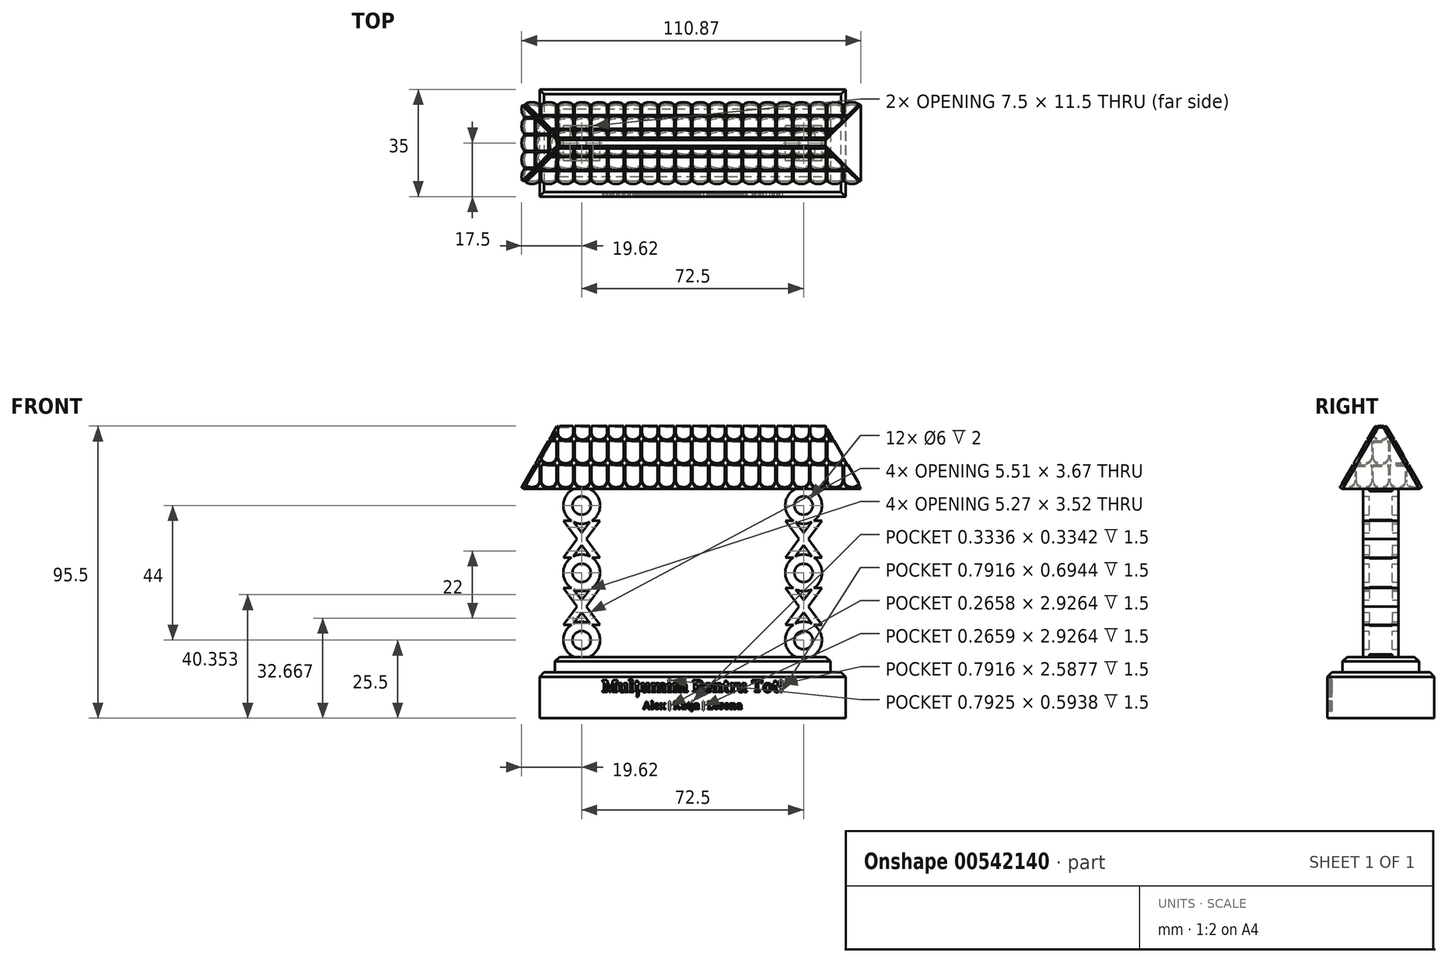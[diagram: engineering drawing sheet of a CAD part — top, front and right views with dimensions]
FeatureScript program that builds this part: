
annotation { "Feature Type Name" : "Feature", "Feature Type Description" : "" }
export const myFeature = defineFeature(function(context is Context, id is Id, definition is map)
    precondition{}
    {
        {
            var Q0;
            Q0=qCreatedBy(makeId("Top.planeOp"),FACE);
            var sketch = newSketch(context, id + "F0", { "sketchPlane" : qUnion([Q0])});
            skLineSegment(sketch, "E0.bottom", {"start": v(0, 0) * mm, "end": v(-100, 0) * mm});
            skLineSegment(sketch, "E0.top", {"start": v(0, 35) * mm, "end": v(-100, 35) * mm});
            skLineSegment(sketch, "E0.left", {"start": v(0, 0) * mm, "end": v(0, 35) * mm});
            skLineSegment(sketch, "E0.right", {"start": v(-100, 0) * mm, "end": v(-100, 35) * mm});
            skSolve(sketch);
        }
        {
            var Q0;
            Q0 = qSketchRegion(id + "F0", true);
            extrude(context, id + "F1", {"entities" : qUnion([Q0]), "depth" : 5 * mm, "offsetDistance" : 25 * mm});
        }
        {
            var Q0;
            Q0=makeQuery(id+"F1.opExtrude","CAP_FACE",FACE,{"disambiguationData":[OSD([sQuery(id+"F0.wireOp",EDGE,"E0.bottom"),sQuery(id+"F0.wireOp",EDGE,"E0.top"),sQuery(id+"F0.wireOp",EDGE,"E0.left"),sQuery(id+"F0.wireOp",EDGE,"E0.right")])],"isStart":false});
            var sketch = newSketch(context, id + "F2", { "sketchPlane" : qUnion([Q0])});
            skLineSegment(sketch, "E1.bottom", {"start": v(-5, 30) * mm, "end": v(-95, 30) * mm});
            skLineSegment(sketch, "E1.top", {"start": v(-5, 5) * mm, "end": v(-95, 5) * mm});
            skLineSegment(sketch, "E1.left", {"start": v(-5, 30) * mm, "end": v(-5, 5) * mm});
            skLineSegment(sketch, "E1.right", {"start": v(-95, 30) * mm, "end": v(-95, 5) * mm});
            skPoint(sketch, "E1.middle", {"position": v(-50, 17.5) * mm});
            skPoint(sketch, "E1.middle.positionSnap0", {"position": v(0, 17.5) * mm});
            skPoint(sketch, "E1.middle.positionSnap1", {"position": v(-50, 35) * mm});
            skPoint(sketch, "E1.centerSnap0", {"position": v(0, 17.5) * mm});
            skPoint(sketch, "E1.centerSnap1", {"position": v(-50, 35) * mm});
            skSolve(sketch);
        }
        {
            var Q0;
            Q0=makeQuery(id+"F2.imprint","IMPRINT",FACE,{"disambiguationData":[TD([[makeQuery(id+"F2.imprint","IMPRINT",EDGE,{"derivedFrom":sQuery(id+"F2.wireOp",EDGE,"E1.bottom")}),1.0]])]});
            extrude(context, id + "F3", {"entities" : qUnion([Q0]), "operationType" : NewBodyOperationType.ADD, "depth" : 5 * mm, "offsetDistance" : 25 * mm});
        }
        {
            var Q0;
            Q0=makeQuery(id+"F3.opExtrude","CAP_FACE",FACE,{"disambiguationData":[OSD([sQuery(id+"F2.wireOp",EDGE,"E1.bottom"),sQuery(id+"F2.wireOp",EDGE,"E1.top"),sQuery(id+"F2.wireOp",EDGE,"E1.left"),sQuery(id+"F2.wireOp",EDGE,"E1.right")])],"isStart":false});
            var sketch = newSketch(context, id + "F4", { "sketchPlane" : qUnion([Q0])});
            skLineSegment(sketch, "E2", {"start": v(-95, 17.5) * mm, "end": v(-5, 17.5) * mm, "construction": true});
            skLineSegment(sketch, "E3.bottom", {"start": v(-82.5, 21.25) * mm, "end": v(-90, 21.25) * mm});
            skLineSegment(sketch, "E3.top", {"start": v(-82.5, 13.75) * mm, "end": v(-90, 13.75) * mm});
            skLineSegment(sketch, "E3.left", {"start": v(-82.5, 21.25) * mm, "end": v(-82.5, 13.75) * mm});
            skLineSegment(sketch, "E3.right", {"start": v(-90, 21.25) * mm, "end": v(-90, 13.75) * mm});
            skPoint(sketch, "E3.middle", {"position": v(-86.25, 17.5) * mm});
            skLineSegment(sketch, "E4", {"start": v(-50, 30) * mm, "end": v(-50, 5) * mm, "construction": true});
            skLineSegment(sketch, "E5.MirrorCS", {"start": v(-17.5, 21.25) * mm, "end": v(-10, 21.25) * mm});
            skLineSegment(sketch, "E6.MirrorCS", {"start": v(-10, 21.25) * mm, "end": v(-10, 13.75) * mm});
            skLineSegment(sketch, "E7.MirrorCS", {"start": v(-17.5, 21.25) * mm, "end": v(-17.5, 13.75) * mm});
            skLineSegment(sketch, "E8.MirrorCS", {"start": v(-17.5, 13.75) * mm, "end": v(-10, 13.75) * mm});
            skSolve(sketch);
        }
        {
            var Q0;
            Q0 = qSketchRegion(id + "F4", true);
            extrude(context, id + "F5", {"entities" : qUnion([Q0]), "operationType" : NewBodyOperationType.ADD, "depth" : 55 * mm, "offsetDistance" : 25 * mm});
        }
        {
            var Q0;
            Q0=makeQuery(id+"F5.opExtrude","CAP_FACE",FACE,{"disambiguationData":[OSD([sQuery(id+"F4.wireOp",EDGE,"E3.bottom"),sQuery(id+"F4.wireOp",EDGE,"E3.top"),sQuery(id+"F4.wireOp",EDGE,"E3.left"),sQuery(id+"F4.wireOp",EDGE,"E3.right")])],"isStart":false});
            var sketch = newSketch(context, id + "F6", { "sketchPlane" : qUnion([Q0])});
            skLineSegment(sketch, "E9.bottom", {"start": v(-105, 30) * mm, "end": v(5, 30) * mm});
            skLineSegment(sketch, "E9.top", {"start": v(-105, 5) * mm, "end": v(5, 5) * mm});
            skLineSegment(sketch, "E9.left", {"start": v(-105, 30) * mm, "end": v(-105, 5) * mm});
            skLineSegment(sketch, "E9.right", {"start": v(5, 30) * mm, "end": v(5, 5) * mm});
            skSolve(sketch);
        }
        {
            var Q0;
            Q0 = qSketchRegion(id + "F6", true);
            extrude(context, id + "F7", {"entities" : qUnion([Q0]), "operationType" : NewBodyOperationType.ADD, "depth" : 20 * mm, "offsetDistance" : 25 * mm, "hasDraft" : true, "draftAngle" : 30 * degree, "draftPullDirection" : true});
        }
        {
            var Q0;
            Q0=makeQuery(id+"F5.opExtrude","SWEPT_FACE",FACE,{"disambiguationData":[OSD([sQuery(id+"F4.wireOp",EDGE,"E3.top")])]});
            var sketch = newSketch(context, id + "F8", { "sketchPlane" : qUnion([Q0])});
            skLineSegment(sketch, "E10", {"start": v(-86.25, 65) * mm, "end": v(-86.25, 10) * mm, "construction": true});
            skArc(sketch, "E11", {"start": v(-88.89, 54.11) * mm, "mid": v(-86.25, 53.5) * mm, "end": v(-83.61, 54.11) * mm});
            skCircle(sketch, "E12", {"center": v(-86.25, 59.5) * mm, "radius": 3 * mm});
            skLineSegment(sketch, "E13", {"start": v(-86.25, 50.6) * mm, "end": v(-88.89, 54.11) * mm});
            skLineSegment(sketch, "E14", {"start": v(-89.57, 54.5) * mm, "end": v(-92.25, 54.5) * mm});
            skLineSegment(sketch, "E15", {"start": v(-92.25, 54.5) * mm, "end": v(-87.75, 48.5) * mm});
            skLineSegment(sketch, "E16", {"start": v(-87.75, 48.5) * mm, "end": v(-92.25, 42.5) * mm});
            skLineSegment(sketch, "E17", {"start": v(-92.25, 42.5) * mm, "end": v(-89.25, 42.5) * mm});
            skLineSegment(sketch, "E18", {"start": v(-89, 42.83) * mm, "end": v(-86.25, 46.5) * mm});
            skLineSegment(sketch, "E19", {"start": v(-92.25, 54.5) * mm, "end": v(-92.25, 59.5) * mm, "construction": true});
            skLineSegment(sketch, "E20", {"start": v(-86.25, 48.5) * mm, "end": v(-94.11, 48.5) * mm, "construction": true});
            skLineSegment(sketch, "E21.MirrorCS", {"start": v(-83.5, 42.83) * mm, "end": v(-86.25, 46.5) * mm});
            skLineSegment(sketch, "E22.MirrorCS", {"start": v(-80.25, 42.5) * mm, "end": v(-82.94, 42.5) * mm});
            skLineSegment(sketch, "E23.MirrorCS", {"start": v(-84.75, 48.5) * mm, "end": v(-80.25, 42.5) * mm});
            skLineSegment(sketch, "E24.MirrorCS", {"start": v(-80.25, 54.5) * mm, "end": v(-84.75, 48.5) * mm});
            skLineSegment(sketch, "E25.MirrorCS", {"start": v(-86.25, 50.6) * mm, "end": v(-83.61, 54.11) * mm});
            skLineSegment(sketch, "E26.MirrorCS", {"start": v(-82.93, 54.5) * mm, "end": v(-80.25, 54.5) * mm});
            skLineSegment(sketch, "E27.0.1.0", {"start": v(-82.93, 32.5) * mm, "end": v(-80.25, 32.5) * mm});
            skLineSegment(sketch, "E27.0.1.1", {"start": v(-92.25, 32.5) * mm, "end": v(-87.75, 26.5) * mm});
            skLineSegment(sketch, "E27.0.1.2", {"start": v(-92.25, 32.5) * mm, "end": v(-92.25, 37.5) * mm, "construction": true});
            skLineSegment(sketch, "E27.0.1.3", {"start": v(-86.25, 26.5) * mm, "end": v(-94.11, 26.5) * mm, "construction": true});
            skLineSegment(sketch, "E27.0.1.4", {"start": v(-83.5, 20.83) * mm, "end": v(-86.25, 24.5) * mm});
            skLineSegment(sketch, "E27.0.1.5", {"start": v(-89, 20.83) * mm, "end": v(-86.25, 24.5) * mm});
            skCircle(sketch, "E27.0.1.6", {"center": v(-86.25, 37.5) * mm, "radius": 3 * mm});
            skLineSegment(sketch, "E27.0.1.7", {"start": v(-84.75, 26.5) * mm, "end": v(-80.25, 20.5) * mm});
            skLineSegment(sketch, "E27.0.1.8", {"start": v(-87.75, 26.5) * mm, "end": v(-92.25, 20.5) * mm});
            skLineSegment(sketch, "E27.0.1.9", {"start": v(-80.25, 20.5) * mm, "end": v(-82.94, 20.5) * mm});
            skLineSegment(sketch, "E27.0.1.10", {"start": v(-80.25, 32.5) * mm, "end": v(-84.75, 26.5) * mm});
            skLineSegment(sketch, "E27.0.1.11", {"start": v(-92.25, 20.5) * mm, "end": v(-89.56, 20.5) * mm});
            skArc(sketch, "E27.0.1.12", {"start": v(-89.56, 42.5) * mm, "mid": v(-92.25, 37.5) * mm, "end": v(-89.57, 32.5) * mm});
            skLineSegment(sketch, "E27.0.1.13", {"start": v(-86.25, 28.6) * mm, "end": v(-88.89, 32.11) * mm});
            skLineSegment(sketch, "E27.0.1.15", {"start": v(-86.25, 28.6) * mm, "end": v(-83.61, 32.11) * mm});
            skLineSegment(sketch, "E27.direction1", {"start": v(-92.25, 42.5) * mm, "end": v(-89.56, 42.5) * mm, "construction": true});
            skLineSegment(sketch, "E27.direction2", {"start": v(-92.25, 42.5) * mm, "end": v(-92.25, 20.5) * mm, "construction": true});
            skArc(sketch, "E28.trimOffspring", {"start": v(-82.93, 54.5) * mm, "mid": v(-86.25, 65.5) * mm, "end": v(-89.57, 54.5) * mm});
            skLineSegment(sketch, "E29.trimOffspring", {"start": v(-89.25, 42.5) * mm, "end": v(-83.25, 42.5) * mm, "construction": true});
            skLineSegment(sketch, "E30.trimOffspring", {"start": v(-82.94, 42.5) * mm, "end": v(-67.25, 42.5) * mm, "construction": true});
            skArc(sketch, "E31.trimOffspring", {"start": v(-83.5, 42.83) * mm, "mid": v(-86.25, 43.5) * mm, "end": v(-89, 42.83) * mm});
            skArc(sketch, "E32.trimOffspring", {"start": v(-82.93, 32.5) * mm, "mid": v(-80.25, 37.5) * mm, "end": v(-82.94, 42.5) * mm});
            skArc(sketch, "E33.trimOffspring", {"start": v(-88.89, 32.11) * mm, "mid": v(-86.25, 31.5) * mm, "end": v(-83.61, 32.11) * mm});
            skLineSegment(sketch, "E34", {"start": v(-89.57, 32.5) * mm, "end": v(-92.25, 32.5) * mm});
            skArc(sketch, "E35", {"start": v(-83.5, 20.83) * mm, "mid": v(-86.25, 21.5) * mm, "end": v(-89, 20.83) * mm});
            skCircle(sketch, "E36", {"center": v(-86.25, 15.5) * mm, "radius": 3 * mm});
            skArc(sketch, "E37.trimOffspring", {"start": v(-89.56, 20.5) * mm, "mid": v(-86.25, 9.5) * mm, "end": v(-82.94, 20.5) * mm});
            skSolve(sketch);
        }
        {
            var Q0;
            Q0 = qSketchRegion(id + "F8", true);
            var Q1;
            Q1=sQuery(id+"F8.wireOp",EDGE,"E11");
            var Q2;
            Q2=sQuery(id+"F8.wireOp",EDGE,"E12");
            var Q3;
            Q3=makeQuery(id+"F5.opExtrude","SWEPT_FACE",FACE,{"disambiguationData":[OSD([sQuery(id+"F4.wireOp",EDGE,"E3.bottom")])]});
            extrude(context, id + "F9", {"entities" : qUnion([Q0]), "operationType" : NewBodyOperationType.ADD, "surfaceEntities" : qUnion([Q1, Q2]), "depth" : 2 * mm, "offsetDistance" : 25 * mm, "hasSecondDirection" : true, "secondDirectionBound" : SecondDirectionBoundingType.UP_TO_SURFACE, "secondDirectionOppositeDirection" : true, "secondDirectionDepth" : 25 * mm, "secondDirectionBoundEntityFace" : qUnion([Q3]), "hasSecondDirectionOffset" : true, "secondDirectionOffsetDistance" : 2 * mm, "secondDirectionOffsetOppositeDirection" : true});
        }
        {
            var Q0;
            Q0=makeQuery(id+"F3.opExtrude","SWEPT_FACE",FACE,{"disambiguationData":[OSD([sQuery(id+"F2.wireOp",EDGE,"E1.right")])]});
            var Q1;
            Q1=makeQuery(id+"F3.opExtrude","SWEPT_FACE",FACE,{"disambiguationData":[OSD([sQuery(id+"F2.wireOp",EDGE,"E1.left")])]});
            cPlane(context, id + "F10", {"entities" : qUnion([Q0, Q1]), "cplaneType" : CPlaneType.MID_PLANE, "offset" : 25 * mm, "width" : 150 * mm, "height" : 150 * mm});
        }
        {
            var Q0;
            Q0=makeQuery(id+"F1.opExtrude","SWEPT_BODY",BODY,{"disambiguationData":[OSD([sQuery(id+"F0.wireOp",EDGE,"E0.bottom"),sQuery(id+"F0.wireOp",EDGE,"E0.top"),sQuery(id+"F0.wireOp",EDGE,"E0.left"),sQuery(id+"F0.wireOp",EDGE,"E0.right")])]});
            var Q1;
            Q1=qCreatedBy(id+"F10.planeOp",FACE);
            mirror(context, id + "F11", {"operationType" : NewBodyOperationType.ADD, "entities" : qUnion([Q0]), "mirrorPlane" : qUnion([Q1])});
        }
        {
            var Q0;
            Q0=makeQuery(id+"F9.boolean.opBoolean","SPLIT",FACE,{"disambiguationData":[TD([makeQuery(id+"F5.opExtrude","SWEPT_FACE",FACE,{"disambiguationData":[OSD([sQuery(id+"F4.wireOp",EDGE,"E3.right")])]}),makeQuery(id+"F9.opExtrude","SWEPT_FACE",FACE,{"disambiguationData":[OSD([sQuery(id+"F8.wireOp",EDGE,"E15")])]}),makeQuery(id+"F9.opExtrude","SWEPT_FACE",FACE,{"disambiguationData":[OSD([sQuery(id+"F8.wireOp",EDGE,"E16")])]})])],"derivedFrom":makeQuery(id+"F5.opExtrude","SWEPT_FACE",FACE,{"disambiguationData":[OSD([sQuery(id+"F4.wireOp",EDGE,"E3.top")])]})});
            var sketch = newSketch(context, id + "F12", { "sketchPlane" : qUnion([Q0])});
            skLineSegment(sketch, "E38", {"start": v(-90, 51.5) * mm, "end": v(-87.75, 48.5) * mm});
            skLineSegment(sketch, "E39", {"start": v(-87.75, 48.5) * mm, "end": v(-90, 45.5) * mm});
            skLineSegment(sketch, "E40", {"start": v(-90, 45.5) * mm, "end": v(-90, 51.5) * mm});
            skLineSegment(sketch, "E41", {"start": v(-87.75, 26.5) * mm, "end": v(-90, 29.5) * mm});
            skLineSegment(sketch, "E42", {"start": v(-90, 29.5) * mm, "end": v(-90, 23.5) * mm});
            skLineSegment(sketch, "E43", {"start": v(-90, 23.5) * mm, "end": v(-87.75, 26.5) * mm});
            skLineSegment(sketch, "E44", {"start": v(-86.25, 59.5) * mm, "end": v(-86.25, 15.5) * mm, "construction": true});
            skLineSegment(sketch, "E45.MirrorCS", {"start": v(-82.5, 23.5) * mm, "end": v(-84.75, 26.5) * mm});
            skLineSegment(sketch, "E46.MirrorCS", {"start": v(-82.5, 29.5) * mm, "end": v(-82.5, 23.5) * mm});
            skLineSegment(sketch, "E47.MirrorCS", {"start": v(-84.75, 26.5) * mm, "end": v(-82.5, 29.5) * mm});
            skLineSegment(sketch, "E48.MirrorCS", {"start": v(-82.5, 45.5) * mm, "end": v(-82.5, 51.5) * mm});
            skLineSegment(sketch, "E49.MirrorCS", {"start": v(-82.5, 51.5) * mm, "end": v(-84.75, 48.5) * mm});
            skLineSegment(sketch, "E50.MirrorCS", {"start": v(-84.75, 48.5) * mm, "end": v(-82.5, 45.5) * mm});
            skLineSegment(sketch, "E51", {"start": v(-50, 62.04) * mm, "end": v(-50, 26.06) * mm, "construction": true});
            skLineSegment(sketch, "E52.MirrorCS", {"start": v(-15.25, 26.5) * mm, "end": v(-17.5, 29.5) * mm});
            skLineSegment(sketch, "E53.MirrorCS", {"start": v(-17.5, 23.5) * mm, "end": v(-15.25, 26.5) * mm});
            skLineSegment(sketch, "E54.MirrorCS", {"start": v(-17.5, 29.5) * mm, "end": v(-17.5, 23.5) * mm});
            skLineSegment(sketch, "E55.MirrorCS", {"start": v(-17.5, 45.5) * mm, "end": v(-17.5, 51.5) * mm});
            skLineSegment(sketch, "E56.MirrorCS", {"start": v(-15.25, 48.5) * mm, "end": v(-17.5, 45.5) * mm});
            skLineSegment(sketch, "E57.MirrorCS", {"start": v(-17.5, 51.5) * mm, "end": v(-15.25, 48.5) * mm});
            skLineSegment(sketch, "E58.MirrorCS", {"start": v(-10, 23.5) * mm, "end": v(-12.25, 26.5) * mm});
            skLineSegment(sketch, "E59.MirrorCS", {"start": v(-10, 29.5) * mm, "end": v(-10, 23.5) * mm});
            skLineSegment(sketch, "E60.MirrorCS", {"start": v(-12.25, 26.5) * mm, "end": v(-10, 29.5) * mm});
            skLineSegment(sketch, "E61.MirrorCS", {"start": v(-10, 45.5) * mm, "end": v(-10, 51.5) * mm});
            skLineSegment(sketch, "E62.MirrorCS", {"start": v(-10, 51.5) * mm, "end": v(-12.25, 48.5) * mm});
            skLineSegment(sketch, "E63.MirrorCS", {"start": v(-12.25, 48.5) * mm, "end": v(-10, 45.5) * mm});
            skSolve(sketch);
        }
        {
            var Q0;
            Q0 = qSketchRegion(id + "F12", true);
            extrude(context, id + "F13", {"entities" : qUnion([Q0]), "operationType" : NewBodyOperationType.REMOVE, "oppositeDirection" : true, "depth" : 25 * mm, "offsetDistance" : 25 * mm});
        }
        {
            var Q0;
            Q0=makeQuery(id+"F7.opExtrude","SWEPT_FACE",FACE,{"disambiguationData":[OSD([sQuery(id+"F6.wireOp",EDGE,"E9.top")])]});
            var sketch = newSketch(context, id + "F14", { "sketchPlane" : qUnion([Q0])});
            skArc(sketch, "E64", {"start": v(-104.5, 59.8) * mm, "mid": v(-101.7, 58.92) * mm, "end": v(-100, 61.3) * mm});
            skLineSegment(sketch, "E65", {"start": v(-100, 61.3) * mm, "end": v(-100, 67.3) * mm});
            skLineSegment(sketch, "E66", {"start": v(-105, 61.3) * mm, "end": v(-105, 67.3) * mm});
            skLineSegment(sketch, "E67", {"start": v(-100, 67.3) * mm, "end": v(-100.75, 67.3) * mm});
            skArc(sketch, "E68.0.1.2", {"start": v(-105, 70.3) * mm, "mid": v(-102.5, 67.8) * mm, "end": v(-100, 70.3) * mm, "construction": true});
            skLineSegment(sketch, "E68.1.0.0", {"start": v(-94.5, 67.3) * mm, "end": v(-99.5, 67.3) * mm});
            skLineSegment(sketch, "E68.1.0.1", {"start": v(-94.5, 61.3) * mm, "end": v(-94.5, 67.3) * mm});
            skArc(sketch, "E68.1.0.2", {"start": v(-99.5, 61.3) * mm, "mid": v(-97, 58.8) * mm, "end": v(-94.5, 61.3) * mm});
            skLineSegment(sketch, "E68.1.0.3", {"start": v(-99.5, 61.3) * mm, "end": v(-99.5, 67.3) * mm});
            skLineSegment(sketch, "E68.1.1.0", {"start": v(-94.5, 76.3) * mm, "end": v(-96.25, 76.3) * mm});
            skLineSegment(sketch, "E68.1.1.1", {"start": v(-94.5, 70.3) * mm, "end": v(-94.5, 76.3) * mm});
            skArc(sketch, "E68.1.1.2", {"start": v(-99.46, 69.87) * mm, "mid": v(-96.79, 67.8) * mm, "end": v(-94.5, 70.3) * mm});
            skLineSegment(sketch, "E68.1.2.1", {"start": v(-94.5, 79.3) * mm, "end": v(-94.5, 79.8) * mm});
            skArc(sketch, "E68.1.2.2", {"start": v(-95.86, 77.07) * mm, "mid": v(-94.87, 77.99) * mm, "end": v(-94.5, 79.3) * mm});
            skLineSegment(sketch, "E68.2.0.0", {"start": v(-89, 67.3) * mm, "end": v(-94, 67.3) * mm});
            skLineSegment(sketch, "E68.2.0.1", {"start": v(-89, 61.3) * mm, "end": v(-89, 67.3) * mm});
            skArc(sketch, "E68.2.0.2", {"start": v(-94, 61.3) * mm, "mid": v(-91.5, 58.8) * mm, "end": v(-89, 61.3) * mm});
            skLineSegment(sketch, "E68.2.0.3", {"start": v(-94, 61.3) * mm, "end": v(-94, 67.3) * mm});
            skLineSegment(sketch, "E68.2.1.0", {"start": v(-89, 76.3) * mm, "end": v(-94, 76.3) * mm});
            skLineSegment(sketch, "E68.2.1.1", {"start": v(-89, 70.3) * mm, "end": v(-89, 76.3) * mm});
            skArc(sketch, "E68.2.1.2", {"start": v(-94, 70.3) * mm, "mid": v(-91.5, 67.8) * mm, "end": v(-89, 70.3) * mm});
            skLineSegment(sketch, "E68.2.1.3", {"start": v(-94, 70.3) * mm, "end": v(-94, 76.3) * mm});
            skLineSegment(sketch, "E68.2.2.1", {"start": v(-89, 79.3) * mm, "end": v(-89, 81.89) * mm});
            skArc(sketch, "E68.2.2.2", {"start": v(-94, 79.3) * mm, "mid": v(-91.5, 76.8) * mm, "end": v(-89, 79.3) * mm});
            skLineSegment(sketch, "E68.2.2.3", {"start": v(-94, 79.3) * mm, "end": v(-94, 80.8) * mm});
            skLineSegment(sketch, "E68.3.0.0", {"start": v(-83.5, 67.3) * mm, "end": v(-88.5, 67.3) * mm});
            skLineSegment(sketch, "E68.3.0.1", {"start": v(-83.5, 61.3) * mm, "end": v(-83.5, 67.3) * mm});
            skArc(sketch, "E68.3.0.2", {"start": v(-88.5, 61.3) * mm, "mid": v(-86, 58.8) * mm, "end": v(-83.5, 61.3) * mm});
            skLineSegment(sketch, "E68.3.0.3", {"start": v(-88.5, 61.3) * mm, "end": v(-88.5, 67.3) * mm});
            skLineSegment(sketch, "E68.3.1.0", {"start": v(-83.5, 76.3) * mm, "end": v(-88.5, 76.3) * mm});
            skLineSegment(sketch, "E68.3.1.1", {"start": v(-83.5, 70.3) * mm, "end": v(-83.5, 76.3) * mm});
            skArc(sketch, "E68.3.1.2", {"start": v(-88.5, 70.3) * mm, "mid": v(-86, 67.8) * mm, "end": v(-83.5, 70.3) * mm});
            skLineSegment(sketch, "E68.3.1.3", {"start": v(-88.5, 70.3) * mm, "end": v(-88.5, 76.3) * mm});
            skLineSegment(sketch, "E68.3.2.1", {"start": v(-83.5, 79.3) * mm, "end": v(-83.5, 81.89) * mm});
            skArc(sketch, "E68.3.2.2", {"start": v(-88.5, 79.3) * mm, "mid": v(-86, 76.8) * mm, "end": v(-83.5, 79.3) * mm});
            skLineSegment(sketch, "E68.3.2.3", {"start": v(-88.5, 79.3) * mm, "end": v(-88.5, 81.89) * mm});
            skLineSegment(sketch, "E68.4.0.0", {"start": v(-78, 67.3) * mm, "end": v(-83, 67.3) * mm});
            skLineSegment(sketch, "E68.4.0.1", {"start": v(-78, 61.3) * mm, "end": v(-78, 67.3) * mm});
            skArc(sketch, "E68.4.0.2", {"start": v(-83, 61.3) * mm, "mid": v(-80.5, 58.8) * mm, "end": v(-78, 61.3) * mm});
            skLineSegment(sketch, "E68.4.0.3", {"start": v(-83, 61.3) * mm, "end": v(-83, 67.3) * mm});
            skLineSegment(sketch, "E68.4.1.0", {"start": v(-78, 76.3) * mm, "end": v(-83, 76.3) * mm});
            skLineSegment(sketch, "E68.4.1.1", {"start": v(-78, 70.3) * mm, "end": v(-78, 76.3) * mm});
            skArc(sketch, "E68.4.1.2", {"start": v(-83, 70.3) * mm, "mid": v(-80.5, 67.8) * mm, "end": v(-78, 70.3) * mm});
            skLineSegment(sketch, "E68.4.1.3", {"start": v(-83, 70.3) * mm, "end": v(-83, 76.3) * mm});
            skLineSegment(sketch, "E68.4.2.1", {"start": v(-78, 79.3) * mm, "end": v(-78, 81.89) * mm});
            skArc(sketch, "E68.4.2.2", {"start": v(-83, 79.3) * mm, "mid": v(-80.5, 76.8) * mm, "end": v(-78, 79.3) * mm});
            skLineSegment(sketch, "E68.4.2.3", {"start": v(-83, 79.3) * mm, "end": v(-83, 81.89) * mm});
            skLineSegment(sketch, "E68.5.0.0", {"start": v(-72.5, 67.3) * mm, "end": v(-77.5, 67.3) * mm});
            skLineSegment(sketch, "E68.5.0.1", {"start": v(-72.5, 61.3) * mm, "end": v(-72.5, 67.3) * mm});
            skArc(sketch, "E68.5.0.2", {"start": v(-77.5, 61.3) * mm, "mid": v(-75, 58.8) * mm, "end": v(-72.5, 61.3) * mm});
            skLineSegment(sketch, "E68.5.0.3", {"start": v(-77.5, 61.3) * mm, "end": v(-77.5, 67.3) * mm});
            skLineSegment(sketch, "E68.5.1.0", {"start": v(-72.5, 76.3) * mm, "end": v(-77.5, 76.3) * mm});
            skLineSegment(sketch, "E68.5.1.1", {"start": v(-72.5, 70.3) * mm, "end": v(-72.5, 76.3) * mm});
            skArc(sketch, "E68.5.1.2", {"start": v(-77.5, 70.3) * mm, "mid": v(-75, 67.8) * mm, "end": v(-72.5, 70.3) * mm});
            skLineSegment(sketch, "E68.5.1.3", {"start": v(-77.5, 70.3) * mm, "end": v(-77.5, 76.3) * mm});
            skLineSegment(sketch, "E68.5.2.1", {"start": v(-72.5, 79.3) * mm, "end": v(-72.5, 81.89) * mm});
            skArc(sketch, "E68.5.2.2", {"start": v(-77.5, 79.3) * mm, "mid": v(-75, 76.8) * mm, "end": v(-72.5, 79.3) * mm});
            skLineSegment(sketch, "E68.5.2.3", {"start": v(-77.5, 79.3) * mm, "end": v(-77.5, 81.89) * mm});
            skLineSegment(sketch, "E68.6.0.0", {"start": v(-67, 67.3) * mm, "end": v(-72, 67.3) * mm});
            skLineSegment(sketch, "E68.6.0.1", {"start": v(-67, 61.3) * mm, "end": v(-67, 67.3) * mm});
            skArc(sketch, "E68.6.0.2", {"start": v(-72, 61.3) * mm, "mid": v(-69.5, 58.8) * mm, "end": v(-67, 61.3) * mm});
            skLineSegment(sketch, "E68.6.0.3", {"start": v(-72, 61.3) * mm, "end": v(-72, 67.3) * mm});
            skLineSegment(sketch, "E68.6.1.0", {"start": v(-67, 76.3) * mm, "end": v(-72, 76.3) * mm});
            skLineSegment(sketch, "E68.6.1.1", {"start": v(-67, 70.3) * mm, "end": v(-67, 76.3) * mm});
            skArc(sketch, "E68.6.1.2", {"start": v(-72, 70.3) * mm, "mid": v(-69.5, 67.8) * mm, "end": v(-67, 70.3) * mm});
            skLineSegment(sketch, "E68.6.1.3", {"start": v(-72, 70.3) * mm, "end": v(-72, 76.3) * mm});
            skLineSegment(sketch, "E68.6.2.1", {"start": v(-67, 79.3) * mm, "end": v(-67, 81.89) * mm});
            skArc(sketch, "E68.6.2.2", {"start": v(-72, 79.3) * mm, "mid": v(-69.5, 76.8) * mm, "end": v(-67, 79.3) * mm});
            skLineSegment(sketch, "E68.6.2.3", {"start": v(-72, 79.3) * mm, "end": v(-72, 81.89) * mm});
            skLineSegment(sketch, "E68.7.0.0", {"start": v(-61.5, 67.3) * mm, "end": v(-66.5, 67.3) * mm});
            skLineSegment(sketch, "E68.7.0.1", {"start": v(-61.5, 61.3) * mm, "end": v(-61.5, 67.3) * mm});
            skArc(sketch, "E68.7.0.2", {"start": v(-66.5, 61.3) * mm, "mid": v(-64, 58.8) * mm, "end": v(-61.5, 61.3) * mm});
            skLineSegment(sketch, "E68.7.0.3", {"start": v(-66.5, 61.3) * mm, "end": v(-66.5, 67.3) * mm});
            skLineSegment(sketch, "E68.7.1.0", {"start": v(-61.5, 76.3) * mm, "end": v(-66.5, 76.3) * mm});
            skLineSegment(sketch, "E68.7.1.1", {"start": v(-61.5, 70.3) * mm, "end": v(-61.5, 76.3) * mm});
            skArc(sketch, "E68.7.1.2", {"start": v(-66.5, 70.3) * mm, "mid": v(-64, 67.8) * mm, "end": v(-61.5, 70.3) * mm});
            skLineSegment(sketch, "E68.7.1.3", {"start": v(-66.5, 70.3) * mm, "end": v(-66.5, 76.3) * mm});
            skLineSegment(sketch, "E68.7.2.1", {"start": v(-61.5, 79.3) * mm, "end": v(-61.5, 81.89) * mm});
            skArc(sketch, "E68.7.2.2", {"start": v(-66.5, 79.3) * mm, "mid": v(-64, 76.8) * mm, "end": v(-61.5, 79.3) * mm});
            skLineSegment(sketch, "E68.7.2.3", {"start": v(-66.5, 79.3) * mm, "end": v(-66.5, 81.89) * mm});
            skLineSegment(sketch, "E68.8.0.0", {"start": v(-56, 67.3) * mm, "end": v(-61, 67.3) * mm});
            skLineSegment(sketch, "E68.8.0.1", {"start": v(-56, 61.3) * mm, "end": v(-56, 67.3) * mm});
            skArc(sketch, "E68.8.0.2", {"start": v(-61, 61.3) * mm, "mid": v(-58.5, 58.8) * mm, "end": v(-56, 61.3) * mm});
            skLineSegment(sketch, "E68.8.0.3", {"start": v(-61, 61.3) * mm, "end": v(-61, 67.3) * mm});
            skLineSegment(sketch, "E68.8.1.0", {"start": v(-56, 76.3) * mm, "end": v(-61, 76.3) * mm});
            skLineSegment(sketch, "E68.8.1.1", {"start": v(-56, 70.3) * mm, "end": v(-56, 76.3) * mm});
            skArc(sketch, "E68.8.1.2", {"start": v(-61, 70.3) * mm, "mid": v(-58.5, 67.8) * mm, "end": v(-56, 70.3) * mm});
            skLineSegment(sketch, "E68.8.1.3", {"start": v(-61, 70.3) * mm, "end": v(-61, 76.3) * mm});
            skLineSegment(sketch, "E68.8.2.1", {"start": v(-56, 79.3) * mm, "end": v(-56, 81.89) * mm});
            skArc(sketch, "E68.8.2.2", {"start": v(-61, 79.3) * mm, "mid": v(-58.5, 76.8) * mm, "end": v(-56, 79.3) * mm});
            skLineSegment(sketch, "E68.8.2.3", {"start": v(-61, 79.3) * mm, "end": v(-61, 81.89) * mm});
            skLineSegment(sketch, "E68.9.0.0", {"start": v(-50.5, 67.3) * mm, "end": v(-55.5, 67.3) * mm});
            skLineSegment(sketch, "E68.9.0.1", {"start": v(-50.5, 61.3) * mm, "end": v(-50.5, 67.3) * mm});
            skArc(sketch, "E68.9.0.2", {"start": v(-55.5, 61.3) * mm, "mid": v(-53, 58.8) * mm, "end": v(-50.5, 61.3) * mm});
            skLineSegment(sketch, "E68.9.0.3", {"start": v(-55.5, 61.3) * mm, "end": v(-55.5, 67.3) * mm});
            skLineSegment(sketch, "E68.9.1.0", {"start": v(-50.5, 76.3) * mm, "end": v(-55.5, 76.3) * mm});
            skLineSegment(sketch, "E68.9.1.1", {"start": v(-50.5, 70.3) * mm, "end": v(-50.5, 76.3) * mm});
            skArc(sketch, "E68.9.1.2", {"start": v(-55.5, 70.3) * mm, "mid": v(-53, 67.8) * mm, "end": v(-50.5, 70.3) * mm});
            skLineSegment(sketch, "E68.9.1.3", {"start": v(-55.5, 70.3) * mm, "end": v(-55.5, 76.3) * mm});
            skLineSegment(sketch, "E68.9.2.1", {"start": v(-50.5, 79.3) * mm, "end": v(-50.5, 81.89) * mm});
            skArc(sketch, "E68.9.2.2", {"start": v(-55.5, 79.3) * mm, "mid": v(-53, 76.8) * mm, "end": v(-50.5, 79.3) * mm});
            skLineSegment(sketch, "E68.9.2.3", {"start": v(-55.5, 79.3) * mm, "end": v(-55.5, 81.89) * mm});
            skLineSegment(sketch, "E68.10.0.0", {"start": v(-45, 67.3) * mm, "end": v(-50, 67.3) * mm});
            skLineSegment(sketch, "E68.10.0.1", {"start": v(-45, 61.3) * mm, "end": v(-45, 67.3) * mm});
            skArc(sketch, "E68.10.0.2", {"start": v(-50, 61.3) * mm, "mid": v(-47.5, 58.8) * mm, "end": v(-45, 61.3) * mm});
            skLineSegment(sketch, "E68.10.0.3", {"start": v(-50, 61.3) * mm, "end": v(-50, 67.3) * mm});
            skLineSegment(sketch, "E68.10.1.0", {"start": v(-45, 76.3) * mm, "end": v(-50, 76.3) * mm});
            skLineSegment(sketch, "E68.10.1.1", {"start": v(-45, 70.3) * mm, "end": v(-45, 76.3) * mm});
            skArc(sketch, "E68.10.1.2", {"start": v(-50, 70.3) * mm, "mid": v(-47.5, 67.8) * mm, "end": v(-45, 70.3) * mm});
            skLineSegment(sketch, "E68.10.1.3", {"start": v(-50, 70.3) * mm, "end": v(-50, 76.3) * mm});
            skLineSegment(sketch, "E68.10.2.1", {"start": v(-45, 79.3) * mm, "end": v(-45, 81.89) * mm});
            skArc(sketch, "E68.10.2.2", {"start": v(-50, 79.3) * mm, "mid": v(-47.5, 76.8) * mm, "end": v(-45, 79.3) * mm});
            skLineSegment(sketch, "E68.10.2.3", {"start": v(-50, 79.3) * mm, "end": v(-50, 81.89) * mm});
            skLineSegment(sketch, "E68.11.0.0", {"start": v(-39.5, 67.3) * mm, "end": v(-44.5, 67.3) * mm});
            skLineSegment(sketch, "E68.11.0.1", {"start": v(-39.5, 61.3) * mm, "end": v(-39.5, 67.3) * mm});
            skArc(sketch, "E68.11.0.2", {"start": v(-44.5, 61.3) * mm, "mid": v(-42, 58.8) * mm, "end": v(-39.5, 61.3) * mm});
            skLineSegment(sketch, "E68.11.0.3", {"start": v(-44.5, 61.3) * mm, "end": v(-44.5, 67.3) * mm});
            skLineSegment(sketch, "E68.11.1.0", {"start": v(-39.5, 76.3) * mm, "end": v(-44.5, 76.3) * mm});
            skLineSegment(sketch, "E68.11.1.1", {"start": v(-39.5, 70.3) * mm, "end": v(-39.5, 76.3) * mm});
            skArc(sketch, "E68.11.1.2", {"start": v(-44.5, 70.3) * mm, "mid": v(-42, 67.8) * mm, "end": v(-39.5, 70.3) * mm});
            skLineSegment(sketch, "E68.11.1.3", {"start": v(-44.5, 70.3) * mm, "end": v(-44.5, 76.3) * mm});
            skLineSegment(sketch, "E68.11.2.1", {"start": v(-39.5, 79.3) * mm, "end": v(-39.5, 81.89) * mm});
            skArc(sketch, "E68.11.2.2", {"start": v(-44.5, 79.3) * mm, "mid": v(-42, 76.8) * mm, "end": v(-39.5, 79.3) * mm});
            skLineSegment(sketch, "E68.11.2.3", {"start": v(-44.5, 79.3) * mm, "end": v(-44.5, 81.89) * mm});
            skLineSegment(sketch, "E68.12.0.0", {"start": v(-34, 67.3) * mm, "end": v(-39, 67.3) * mm});
            skLineSegment(sketch, "E68.12.0.1", {"start": v(-34, 61.3) * mm, "end": v(-34, 67.3) * mm});
            skArc(sketch, "E68.12.0.2", {"start": v(-39, 61.3) * mm, "mid": v(-36.5, 58.8) * mm, "end": v(-34, 61.3) * mm});
            skLineSegment(sketch, "E68.12.0.3", {"start": v(-39, 61.3) * mm, "end": v(-39, 67.3) * mm});
            skLineSegment(sketch, "E68.12.1.0", {"start": v(-34, 76.3) * mm, "end": v(-39, 76.3) * mm});
            skLineSegment(sketch, "E68.12.1.1", {"start": v(-34, 70.3) * mm, "end": v(-34, 76.3) * mm});
            skArc(sketch, "E68.12.1.2", {"start": v(-39, 70.3) * mm, "mid": v(-36.5, 67.8) * mm, "end": v(-34, 70.3) * mm});
            skLineSegment(sketch, "E68.12.1.3", {"start": v(-39, 70.3) * mm, "end": v(-39, 76.3) * mm});
            skLineSegment(sketch, "E68.12.2.1", {"start": v(-34, 79.3) * mm, "end": v(-34, 81.89) * mm});
            skArc(sketch, "E68.12.2.2", {"start": v(-39, 79.3) * mm, "mid": v(-36.5, 76.8) * mm, "end": v(-34, 79.3) * mm});
            skLineSegment(sketch, "E68.12.2.3", {"start": v(-39, 79.3) * mm, "end": v(-39, 81.89) * mm});
            skLineSegment(sketch, "E68.13.0.0", {"start": v(-28.5, 67.3) * mm, "end": v(-33.5, 67.3) * mm});
            skLineSegment(sketch, "E68.13.0.1", {"start": v(-28.5, 61.3) * mm, "end": v(-28.5, 67.3) * mm});
            skArc(sketch, "E68.13.0.2", {"start": v(-33.5, 61.3) * mm, "mid": v(-31, 58.8) * mm, "end": v(-28.5, 61.3) * mm});
            skLineSegment(sketch, "E68.13.0.3", {"start": v(-33.5, 61.3) * mm, "end": v(-33.5, 67.3) * mm});
            skLineSegment(sketch, "E68.13.1.0", {"start": v(-28.5, 76.3) * mm, "end": v(-33.5, 76.3) * mm});
            skLineSegment(sketch, "E68.13.1.1", {"start": v(-28.5, 70.3) * mm, "end": v(-28.5, 76.3) * mm});
            skArc(sketch, "E68.13.1.2", {"start": v(-33.5, 70.3) * mm, "mid": v(-31, 67.8) * mm, "end": v(-28.5, 70.3) * mm});
            skLineSegment(sketch, "E68.13.1.3", {"start": v(-33.5, 70.3) * mm, "end": v(-33.5, 76.3) * mm});
            skLineSegment(sketch, "E68.13.2.1", {"start": v(-28.5, 79.3) * mm, "end": v(-28.5, 81.89) * mm});
            skArc(sketch, "E68.13.2.2", {"start": v(-33.5, 79.3) * mm, "mid": v(-31, 76.8) * mm, "end": v(-28.5, 79.3) * mm});
            skLineSegment(sketch, "E68.13.2.3", {"start": v(-33.5, 79.3) * mm, "end": v(-33.5, 81.89) * mm});
            skLineSegment(sketch, "E68.14.0.0", {"start": v(-23, 67.3) * mm, "end": v(-28, 67.3) * mm});
            skLineSegment(sketch, "E68.14.0.1", {"start": v(-23, 61.3) * mm, "end": v(-23, 67.3) * mm});
            skArc(sketch, "E68.14.0.2", {"start": v(-28, 61.3) * mm, "mid": v(-25.5, 58.8) * mm, "end": v(-23, 61.3) * mm});
            skLineSegment(sketch, "E68.14.0.3", {"start": v(-28, 61.3) * mm, "end": v(-28, 67.3) * mm});
            skLineSegment(sketch, "E68.14.1.0", {"start": v(-23, 76.3) * mm, "end": v(-28, 76.3) * mm});
            skLineSegment(sketch, "E68.14.1.1", {"start": v(-23, 70.3) * mm, "end": v(-23, 76.3) * mm});
            skArc(sketch, "E68.14.1.2", {"start": v(-28, 70.3) * mm, "mid": v(-25.5, 67.8) * mm, "end": v(-23, 70.3) * mm});
            skLineSegment(sketch, "E68.14.1.3", {"start": v(-28, 70.3) * mm, "end": v(-28, 76.3) * mm});
            skLineSegment(sketch, "E68.14.2.1", {"start": v(-23, 79.3) * mm, "end": v(-23, 81.89) * mm});
            skArc(sketch, "E68.14.2.2", {"start": v(-28, 79.3) * mm, "mid": v(-25.5, 76.8) * mm, "end": v(-23, 79.3) * mm});
            skLineSegment(sketch, "E68.14.2.3", {"start": v(-28, 79.3) * mm, "end": v(-28, 81.89) * mm});
            skLineSegment(sketch, "E68.15.0.0", {"start": v(-17.5, 67.3) * mm, "end": v(-22.5, 67.3) * mm});
            skLineSegment(sketch, "E68.15.0.1", {"start": v(-17.5, 61.3) * mm, "end": v(-17.5, 67.3) * mm});
            skArc(sketch, "E68.15.0.2", {"start": v(-22.5, 61.3) * mm, "mid": v(-20, 58.8) * mm, "end": v(-17.5, 61.3) * mm});
            skLineSegment(sketch, "E68.15.0.3", {"start": v(-22.5, 61.3) * mm, "end": v(-22.5, 67.3) * mm});
            skLineSegment(sketch, "E68.15.1.0", {"start": v(-17.5, 76.3) * mm, "end": v(-22.5, 76.3) * mm});
            skLineSegment(sketch, "E68.15.1.1", {"start": v(-17.5, 70.3) * mm, "end": v(-17.5, 76.3) * mm});
            skArc(sketch, "E68.15.1.2", {"start": v(-22.5, 70.3) * mm, "mid": v(-20, 67.8) * mm, "end": v(-17.5, 70.3) * mm});
            skLineSegment(sketch, "E68.15.1.3", {"start": v(-22.5, 70.3) * mm, "end": v(-22.5, 76.3) * mm});
            skLineSegment(sketch, "E68.15.2.1", {"start": v(-17.5, 79.3) * mm, "end": v(-17.5, 81.89) * mm});
            skArc(sketch, "E68.15.2.2", {"start": v(-22.5, 79.3) * mm, "mid": v(-20, 76.8) * mm, "end": v(-17.5, 79.3) * mm});
            skLineSegment(sketch, "E68.15.2.3", {"start": v(-22.5, 79.3) * mm, "end": v(-22.5, 81.89) * mm});
            skLineSegment(sketch, "E68.16.0.0", {"start": v(-12, 67.3) * mm, "end": v(-17, 67.3) * mm});
            skLineSegment(sketch, "E68.16.0.1", {"start": v(-12, 61.3) * mm, "end": v(-12, 67.3) * mm});
            skArc(sketch, "E68.16.0.2", {"start": v(-17, 61.3) * mm, "mid": v(-14.5, 58.8) * mm, "end": v(-12, 61.3) * mm});
            skLineSegment(sketch, "E68.16.0.3", {"start": v(-17, 61.3) * mm, "end": v(-17, 67.3) * mm});
            skLineSegment(sketch, "E68.16.1.0", {"start": v(-12, 76.3) * mm, "end": v(-17, 76.3) * mm});
            skLineSegment(sketch, "E68.16.1.1", {"start": v(-12, 70.3) * mm, "end": v(-12, 76.3) * mm});
            skArc(sketch, "E68.16.1.2", {"start": v(-17, 70.3) * mm, "mid": v(-14.5, 67.8) * mm, "end": v(-12, 70.3) * mm});
            skLineSegment(sketch, "E68.16.1.3", {"start": v(-17, 70.3) * mm, "end": v(-17, 76.3) * mm});
            skLineSegment(sketch, "E68.16.2.1", {"start": v(-12, 79.3) * mm, "end": v(-12, 81.89) * mm});
            skArc(sketch, "E68.16.2.2", {"start": v(-17, 79.3) * mm, "mid": v(-14.5, 76.8) * mm, "end": v(-12, 79.3) * mm});
            skLineSegment(sketch, "E68.16.2.3", {"start": v(-17, 79.3) * mm, "end": v(-17, 81.89) * mm});
            skLineSegment(sketch, "E68.17.0.0", {"start": v(-6.5, 67.3) * mm, "end": v(-11.5, 67.3) * mm});
            skLineSegment(sketch, "E68.17.0.1", {"start": v(-6.5, 61.3) * mm, "end": v(-6.5, 67.3) * mm});
            skArc(sketch, "E68.17.0.2", {"start": v(-11.5, 61.3) * mm, "mid": v(-9, 58.8) * mm, "end": v(-6.5, 61.3) * mm});
            skLineSegment(sketch, "E68.17.0.3", {"start": v(-11.5, 61.3) * mm, "end": v(-11.5, 67.3) * mm});
            skLineSegment(sketch, "E68.17.1.0", {"start": v(-6.5, 76.3) * mm, "end": v(-11.5, 76.3) * mm});
            skLineSegment(sketch, "E68.17.1.1", {"start": v(-6.5, 70.3) * mm, "end": v(-6.5, 76.3) * mm});
            skArc(sketch, "E68.17.1.2", {"start": v(-11.5, 70.3) * mm, "mid": v(-9, 67.8) * mm, "end": v(-6.5, 70.3) * mm});
            skLineSegment(sketch, "E68.17.1.3", {"start": v(-11.5, 70.3) * mm, "end": v(-11.5, 76.3) * mm});
            skLineSegment(sketch, "E68.17.2.1", {"start": v(-6.5, 79.3) * mm, "end": v(-6.5, 81.8) * mm});
            skArc(sketch, "E68.17.2.2", {"start": v(-11.5, 79.3) * mm, "mid": v(-9, 76.8) * mm, "end": v(-6.5, 79.3) * mm});
            skLineSegment(sketch, "E68.17.2.3", {"start": v(-11.5, 79.3) * mm, "end": v(-11.5, 81.89) * mm});
            skLineSegment(sketch, "E68.18.0.0", {"start": v(-1, 67.3) * mm, "end": v(-6, 67.3) * mm});
            skLineSegment(sketch, "E68.18.0.1", {"start": v(-1, 61.3) * mm, "end": v(-1, 67.3) * mm});
            skArc(sketch, "E68.18.0.2", {"start": v(-6, 61.3) * mm, "mid": v(-3.5, 58.8) * mm, "end": v(-1, 61.3) * mm});
            skLineSegment(sketch, "E68.18.0.3", {"start": v(-6, 61.3) * mm, "end": v(-6, 67.3) * mm});
            skLineSegment(sketch, "E68.18.1.0", {"start": v(-3.75, 76.3) * mm, "end": v(-6, 76.3) * mm});
            skLineSegment(sketch, "E68.18.1.1", {"start": v(-1, 70.3) * mm, "end": v(-1, 70.8) * mm});
            skArc(sketch, "E68.18.1.2", {"start": v(-6, 70.3) * mm, "mid": v(-3.5, 67.8) * mm, "end": v(-1, 70.3) * mm});
            skLineSegment(sketch, "E68.18.1.3", {"start": v(-6, 70.3) * mm, "end": v(-6, 76.3) * mm});
            skArc(sketch, "E68.18.2.2", {"start": v(-6, 79.3) * mm, "mid": v(-5.45, 77.72) * mm, "end": v(-4.03, 76.85) * mm});
            skLineSegment(sketch, "E68.18.2.3", {"start": v(-6, 79.3) * mm, "end": v(-6, 80.8) * mm});
            skLineSegment(sketch, "E68.19.0.0", {"start": v(0.75, 67.3) * mm, "end": v(-0.5, 67.3) * mm});
            skArc(sketch, "E68.19.0.2", {"start": v(-0.5, 61.3) * mm, "mid": v(1.47, 58.85) * mm, "end": v(4.27, 60.25) * mm});
            skLineSegment(sketch, "E68.19.0.3", {"start": v(-0.5, 61.3) * mm, "end": v(-0.5, 67.3) * mm});
            skLineSegment(sketch, "E68.direction1", {"start": v(-105, 61.3) * mm, "end": v(-99.5, 61.3) * mm, "construction": true});
            skLineSegment(sketch, "E68.direction2", {"start": v(-105, 61.3) * mm, "end": v(-105, 70.3) * mm, "construction": true});
            skLineSegment(sketch, "E69", {"start": v(-105, 58.8) * mm, "end": v(-93.45, 81.89) * mm});
            skLineSegment(sketch, "E70", {"start": v(-93.45, 81.89) * mm, "end": v(-6.55, 81.89) * mm});
            skLineSegment(sketch, "E71", {"start": v(-6.55, 81.89) * mm, "end": v(5, 58.8) * mm});
            skLineSegment(sketch, "E72", {"start": v(5, 58.8) * mm, "end": v(-105, 58.8) * mm});
            skSolve(sketch);
        }
        {
            var Q0;
            {var subQ4=sQuery(id+"F14.wireOp",EDGE,"E68.2.2.1");Q0=makeQuery(id+"F14.imprint","IMPRINT",FACE,{"disambiguationData":[TD([[makeQuery(id+"F14.imprint","IMPRINT",EDGE,{"derivedFrom":subQ4}),1.0]])]});}
            var Q1;
            {var subQ0=sQuery(id+"F14.wireOp",EDGE,"E68.3.2.1");Q1=makeQuery(id+"F14.imprint","IMPRINT",FACE,{"disambiguationData":[TD([[makeQuery(id+"F14.imprint","IMPRINT",EDGE,{"derivedFrom":subQ0}),1.0]])]});}
            var Q2;
            {var subQ0=sQuery(id+"F14.wireOp",EDGE,"E68.4.2.1");Q2=makeQuery(id+"F14.imprint","IMPRINT",FACE,{"disambiguationData":[TD([[makeQuery(id+"F14.imprint","IMPRINT",EDGE,{"derivedFrom":subQ0}),1.0]])]});}
            var Q3;
            {var subQ0=sQuery(id+"F14.wireOp",EDGE,"E68.5.2.1");Q3=makeQuery(id+"F14.imprint","IMPRINT",FACE,{"disambiguationData":[TD([[makeQuery(id+"F14.imprint","IMPRINT",EDGE,{"derivedFrom":subQ0}),1.0]])]});}
            var Q4;
            {var subQ0=sQuery(id+"F14.wireOp",EDGE,"E68.6.2.1");Q4=makeQuery(id+"F14.imprint","IMPRINT",FACE,{"disambiguationData":[TD([[makeQuery(id+"F14.imprint","IMPRINT",EDGE,{"derivedFrom":subQ0}),1.0]])]});}
            var Q5;
            {var subQ0=sQuery(id+"F14.wireOp",EDGE,"E68.7.2.1");Q5=makeQuery(id+"F14.imprint","IMPRINT",FACE,{"disambiguationData":[TD([[makeQuery(id+"F14.imprint","IMPRINT",EDGE,{"derivedFrom":subQ0}),1.0]])]});}
            var Q6;
            {var subQ0=sQuery(id+"F14.wireOp",EDGE,"E68.8.2.1");Q6=makeQuery(id+"F14.imprint","IMPRINT",FACE,{"disambiguationData":[TD([[makeQuery(id+"F14.imprint","IMPRINT",EDGE,{"derivedFrom":subQ0}),1.0]])]});}
            var Q7;
            {var subQ0=sQuery(id+"F14.wireOp",EDGE,"E68.9.2.1");Q7=makeQuery(id+"F14.imprint","IMPRINT",FACE,{"disambiguationData":[TD([[makeQuery(id+"F14.imprint","IMPRINT",EDGE,{"derivedFrom":subQ0}),1.0]])]});}
            var Q8;
            {var subQ0=sQuery(id+"F14.wireOp",EDGE,"E68.10.2.1");Q8=makeQuery(id+"F14.imprint","IMPRINT",FACE,{"disambiguationData":[TD([[makeQuery(id+"F14.imprint","IMPRINT",EDGE,{"derivedFrom":subQ0}),1.0]])]});}
            var Q9;
            {var subQ0=sQuery(id+"F14.wireOp",EDGE,"E68.11.2.1");Q9=makeQuery(id+"F14.imprint","IMPRINT",FACE,{"disambiguationData":[TD([[makeQuery(id+"F14.imprint","IMPRINT",EDGE,{"derivedFrom":subQ0}),1.0]])]});}
            var Q10;
            {var subQ0=sQuery(id+"F14.wireOp",EDGE,"E68.12.2.1");Q10=makeQuery(id+"F14.imprint","IMPRINT",FACE,{"disambiguationData":[TD([[makeQuery(id+"F14.imprint","IMPRINT",EDGE,{"derivedFrom":subQ0}),1.0]])]});}
            var Q11;
            {var subQ0=sQuery(id+"F14.wireOp",EDGE,"E68.13.2.1");Q11=makeQuery(id+"F14.imprint","IMPRINT",FACE,{"disambiguationData":[TD([[makeQuery(id+"F14.imprint","IMPRINT",EDGE,{"derivedFrom":subQ0}),1.0]])]});}
            var Q12;
            {var subQ0=sQuery(id+"F14.wireOp",EDGE,"E68.14.2.1");Q12=makeQuery(id+"F14.imprint","IMPRINT",FACE,{"disambiguationData":[TD([[makeQuery(id+"F14.imprint","IMPRINT",EDGE,{"derivedFrom":subQ0}),1.0]])]});}
            var Q13;
            {var subQ0=sQuery(id+"F14.wireOp",EDGE,"E68.15.2.1");Q13=makeQuery(id+"F14.imprint","IMPRINT",FACE,{"disambiguationData":[TD([[makeQuery(id+"F14.imprint","IMPRINT",EDGE,{"derivedFrom":subQ0}),1.0]])]});}
            var Q14;
            {var subQ0=sQuery(id+"F14.wireOp",EDGE,"E68.1.1.0");Q14=makeQuery(id+"F14.imprint","IMPRINT",FACE,{"disambiguationData":[TD([[makeQuery(id+"F14.imprint","IMPRINT",EDGE,{"derivedFrom":subQ0}),1.0]])]});}
            var Q15;
            Q15=makeQuery(id+"F14.imprint","IMPRINT",FACE,{"disambiguationData":[TD([[makeQuery(id+"F14.imprint","IMPRINT",EDGE,{"derivedFrom":sQuery(id+"F14.wireOp",EDGE,"E68.2.1.0")}),1.0]])]});
            var Q16;
            Q16=makeQuery(id+"F14.imprint","IMPRINT",FACE,{"disambiguationData":[TD([[makeQuery(id+"F14.imprint","IMPRINT",EDGE,{"derivedFrom":sQuery(id+"F14.wireOp",EDGE,"E68.3.1.0")}),1.0]])]});
            var Q17;
            Q17=makeQuery(id+"F14.imprint","IMPRINT",FACE,{"disambiguationData":[TD([[makeQuery(id+"F14.imprint","IMPRINT",EDGE,{"derivedFrom":sQuery(id+"F14.wireOp",EDGE,"E68.4.1.0")}),1.0]])]});
            var Q18;
            Q18=makeQuery(id+"F14.imprint","IMPRINT",FACE,{"disambiguationData":[TD([[makeQuery(id+"F14.imprint","IMPRINT",EDGE,{"derivedFrom":sQuery(id+"F14.wireOp",EDGE,"E68.5.1.0")}),1.0]])]});
            var Q19;
            Q19=makeQuery(id+"F14.imprint","IMPRINT",FACE,{"disambiguationData":[TD([[makeQuery(id+"F14.imprint","IMPRINT",EDGE,{"derivedFrom":sQuery(id+"F14.wireOp",EDGE,"E68.6.1.0")}),1.0]])]});
            var Q20;
            Q20=makeQuery(id+"F14.imprint","IMPRINT",FACE,{"disambiguationData":[TD([[makeQuery(id+"F14.imprint","IMPRINT",EDGE,{"derivedFrom":sQuery(id+"F14.wireOp",EDGE,"E68.7.1.0")}),1.0]])]});
            var Q21;
            Q21=makeQuery(id+"F14.imprint","IMPRINT",FACE,{"disambiguationData":[TD([[makeQuery(id+"F14.imprint","IMPRINT",EDGE,{"derivedFrom":sQuery(id+"F14.wireOp",EDGE,"E68.8.1.0")}),1.0]])]});
            var Q22;
            Q22=makeQuery(id+"F14.imprint","IMPRINT",FACE,{"disambiguationData":[TD([[makeQuery(id+"F14.imprint","IMPRINT",EDGE,{"derivedFrom":sQuery(id+"F14.wireOp",EDGE,"E68.9.1.0")}),1.0]])]});
            var Q23;
            Q23=makeQuery(id+"F14.imprint","IMPRINT",FACE,{"disambiguationData":[TD([[makeQuery(id+"F14.imprint","IMPRINT",EDGE,{"derivedFrom":sQuery(id+"F14.wireOp",EDGE,"E68.10.1.0")}),1.0]])]});
            var Q24;
            Q24=makeQuery(id+"F14.imprint","IMPRINT",FACE,{"disambiguationData":[TD([[makeQuery(id+"F14.imprint","IMPRINT",EDGE,{"derivedFrom":sQuery(id+"F14.wireOp",EDGE,"E68.11.1.0")}),1.0]])]});
            var Q25;
            Q25=makeQuery(id+"F14.imprint","IMPRINT",FACE,{"disambiguationData":[TD([[makeQuery(id+"F14.imprint","IMPRINT",EDGE,{"derivedFrom":sQuery(id+"F14.wireOp",EDGE,"E68.12.1.0")}),1.0]])]});
            var Q26;
            Q26=makeQuery(id+"F14.imprint","IMPRINT",FACE,{"disambiguationData":[TD([[makeQuery(id+"F14.imprint","IMPRINT",EDGE,{"derivedFrom":sQuery(id+"F14.wireOp",EDGE,"E68.13.1.0")}),1.0]])]});
            var Q27;
            Q27=makeQuery(id+"F14.imprint","IMPRINT",FACE,{"disambiguationData":[TD([[makeQuery(id+"F14.imprint","IMPRINT",EDGE,{"derivedFrom":sQuery(id+"F14.wireOp",EDGE,"E68.14.1.0")}),1.0]])]});
            var Q28;
            Q28=makeQuery(id+"F14.imprint","IMPRINT",FACE,{"disambiguationData":[TD([[makeQuery(id+"F14.imprint","IMPRINT",EDGE,{"derivedFrom":sQuery(id+"F14.wireOp",EDGE,"E68.15.1.0")}),1.0]])]});
            var Q29;
            {var subQ1=sQuery(id+"F14.wireOp",EDGE,"E65");Q29=makeQuery(id+"F14.imprint","IMPRINT",FACE,{"disambiguationData":[TD([[makeQuery(id+"F14.imprint","IMPRINT",EDGE,{"derivedFrom":subQ1}),1.0]])]});}
            var Q30;
            Q30=makeQuery(id+"F14.imprint","IMPRINT",FACE,{"disambiguationData":[TD([[makeQuery(id+"F14.imprint","IMPRINT",EDGE,{"derivedFrom":sQuery(id+"F14.wireOp",EDGE,"E68.1.0.0")}),1.0]])]});
            var Q31;
            Q31=makeQuery(id+"F14.imprint","IMPRINT",FACE,{"disambiguationData":[TD([[makeQuery(id+"F14.imprint","IMPRINT",EDGE,{"derivedFrom":sQuery(id+"F14.wireOp",EDGE,"E68.2.0.0")}),1.0]])]});
            var Q32;
            Q32=makeQuery(id+"F14.imprint","IMPRINT",FACE,{"disambiguationData":[TD([[makeQuery(id+"F14.imprint","IMPRINT",EDGE,{"derivedFrom":sQuery(id+"F14.wireOp",EDGE,"E68.3.0.0")}),1.0]])]});
            var Q33;
            Q33=makeQuery(id+"F14.imprint","IMPRINT",FACE,{"disambiguationData":[TD([[makeQuery(id+"F14.imprint","IMPRINT",EDGE,{"derivedFrom":sQuery(id+"F14.wireOp",EDGE,"E68.4.0.0")}),1.0]])]});
            var Q34;
            Q34=makeQuery(id+"F14.imprint","IMPRINT",FACE,{"disambiguationData":[TD([[makeQuery(id+"F14.imprint","IMPRINT",EDGE,{"derivedFrom":sQuery(id+"F14.wireOp",EDGE,"E68.5.0.0")}),1.0]])]});
            var Q35;
            Q35=makeQuery(id+"F14.imprint","IMPRINT",FACE,{"disambiguationData":[TD([[makeQuery(id+"F14.imprint","IMPRINT",EDGE,{"derivedFrom":sQuery(id+"F14.wireOp",EDGE,"E68.6.0.0")}),1.0]])]});
            var Q36;
            Q36=makeQuery(id+"F14.imprint","IMPRINT",FACE,{"disambiguationData":[TD([[makeQuery(id+"F14.imprint","IMPRINT",EDGE,{"derivedFrom":sQuery(id+"F14.wireOp",EDGE,"E68.7.0.0")}),1.0]])]});
            var Q37;
            Q37=makeQuery(id+"F14.imprint","IMPRINT",FACE,{"disambiguationData":[TD([[makeQuery(id+"F14.imprint","IMPRINT",EDGE,{"derivedFrom":sQuery(id+"F14.wireOp",EDGE,"E68.8.0.0")}),1.0]])]});
            var Q38;
            Q38=makeQuery(id+"F14.imprint","IMPRINT",FACE,{"disambiguationData":[TD([[makeQuery(id+"F14.imprint","IMPRINT",EDGE,{"derivedFrom":sQuery(id+"F14.wireOp",EDGE,"E68.9.0.0")}),1.0]])]});
            var Q39;
            Q39=makeQuery(id+"F14.imprint","IMPRINT",FACE,{"disambiguationData":[TD([[makeQuery(id+"F14.imprint","IMPRINT",EDGE,{"derivedFrom":sQuery(id+"F14.wireOp",EDGE,"E68.10.0.0")}),1.0]])]});
            var Q40;
            Q40=makeQuery(id+"F14.imprint","IMPRINT",FACE,{"disambiguationData":[TD([[makeQuery(id+"F14.imprint","IMPRINT",EDGE,{"derivedFrom":sQuery(id+"F14.wireOp",EDGE,"E68.11.0.0")}),1.0]])]});
            var Q41;
            Q41=makeQuery(id+"F14.imprint","IMPRINT",FACE,{"disambiguationData":[TD([[makeQuery(id+"F14.imprint","IMPRINT",EDGE,{"derivedFrom":sQuery(id+"F14.wireOp",EDGE,"E68.12.0.0")}),1.0]])]});
            var Q42;
            Q42=makeQuery(id+"F14.imprint","IMPRINT",FACE,{"disambiguationData":[TD([[makeQuery(id+"F14.imprint","IMPRINT",EDGE,{"derivedFrom":sQuery(id+"F14.wireOp",EDGE,"E68.13.0.0")}),1.0]])]});
            var Q43;
            Q43=makeQuery(id+"F14.imprint","IMPRINT",FACE,{"disambiguationData":[TD([[makeQuery(id+"F14.imprint","IMPRINT",EDGE,{"derivedFrom":sQuery(id+"F14.wireOp",EDGE,"E68.14.0.0")}),1.0]])]});
            var Q44;
            Q44=makeQuery(id+"F14.imprint","IMPRINT",FACE,{"disambiguationData":[TD([[makeQuery(id+"F14.imprint","IMPRINT",EDGE,{"derivedFrom":sQuery(id+"F14.wireOp",EDGE,"E68.15.0.0")}),1.0]])]});
            var Q45;
            {var subQ0=sQuery(id+"F14.wireOp",EDGE,"E68.16.2.1");Q45=makeQuery(id+"F14.imprint","IMPRINT",FACE,{"disambiguationData":[TD([[makeQuery(id+"F14.imprint","IMPRINT",EDGE,{"derivedFrom":subQ0}),1.0]])]});}
            var Q46;
            {var subQ4=sQuery(id+"F14.wireOp",EDGE,"E68.17.2.1");Q46=makeQuery(id+"F14.imprint","IMPRINT",FACE,{"disambiguationData":[TD([[makeQuery(id+"F14.imprint","IMPRINT",EDGE,{"derivedFrom":subQ4}),1.0]])]});}
            var Q47;
            {var subQ0=sQuery(id+"F14.wireOp",EDGE,"E68.18.2.2");Q47=makeQuery(id+"F14.imprint","IMPRINT",FACE,{"disambiguationData":[TD([[makeQuery(id+"F14.imprint","IMPRINT",EDGE,{"derivedFrom":subQ0}),1.0]])]});}
            var Q48;
            Q48=makeQuery(id+"F14.imprint","IMPRINT",FACE,{"disambiguationData":[TD([[makeQuery(id+"F14.imprint","IMPRINT",EDGE,{"derivedFrom":sQuery(id+"F14.wireOp",EDGE,"E68.16.1.0")}),1.0]])]});
            var Q49;
            Q49=makeQuery(id+"F14.imprint","IMPRINT",FACE,{"disambiguationData":[TD([[makeQuery(id+"F14.imprint","IMPRINT",EDGE,{"derivedFrom":sQuery(id+"F14.wireOp",EDGE,"E68.17.1.0")}),1.0]])]});
            var Q50;
            {var subQ1=sQuery(id+"F14.wireOp",EDGE,"E68.18.1.0");Q50=makeQuery(id+"F14.imprint","IMPRINT",FACE,{"disambiguationData":[TD([[makeQuery(id+"F14.imprint","IMPRINT",EDGE,{"derivedFrom":subQ1}),1.0]])]});}
            var Q51;
            Q51=makeQuery(id+"F14.imprint","IMPRINT",FACE,{"disambiguationData":[TD([[makeQuery(id+"F14.imprint","IMPRINT",EDGE,{"derivedFrom":sQuery(id+"F14.wireOp",EDGE,"E68.16.0.0")}),1.0]])]});
            var Q52;
            Q52=makeQuery(id+"F14.imprint","IMPRINT",FACE,{"disambiguationData":[TD([[makeQuery(id+"F14.imprint","IMPRINT",EDGE,{"derivedFrom":sQuery(id+"F14.wireOp",EDGE,"E68.17.0.0")}),1.0]])]});
            var Q53;
            Q53=makeQuery(id+"F14.imprint","IMPRINT",FACE,{"disambiguationData":[TD([[makeQuery(id+"F14.imprint","IMPRINT",EDGE,{"derivedFrom":sQuery(id+"F14.wireOp",EDGE,"E68.18.0.0")}),1.0]])]});
            var Q54;
            {var subQ5=sQuery(id+"F14.wireOp",EDGE,"E68.19.0.0");Q54=makeQuery(id+"F14.imprint","IMPRINT",FACE,{"disambiguationData":[TD([[makeQuery(id+"F14.imprint","IMPRINT",EDGE,{"derivedFrom":subQ5}),1.0]])]});}
            var Q55;
            {var subQ0=sQuery(id+"F14.wireOp",EDGE,"E68.1.2.1");Q55=makeQuery(id+"F14.imprint","IMPRINT",FACE,{"disambiguationData":[TD([[makeQuery(id+"F14.imprint","IMPRINT",EDGE,{"derivedFrom":subQ0}),1.0]])]});}
            extrude(context, id + "F15", {"entities" : qUnion([Q0, Q1, Q2, Q3, Q4, Q5, Q6, Q7, Q8, Q9, Q10, Q11, Q12, Q13, Q14, Q15, Q16, Q17, Q18, Q19, Q20, Q21, Q22, Q23, Q24, Q25, Q26, Q27, Q28, Q29, Q30, Q31, Q32, Q33, Q34, Q35, Q36, Q37, Q38, Q39, Q40, Q41, Q42, Q43, Q44, Q45, Q46, Q47, Q48, Q49, Q50, Q51, Q52, Q53, Q54, Q55]), "operationType" : NewBodyOperationType.ADD, "depth" : 1 * mm, "offsetDistance" : 25 * mm});
        }
        {
            var Q0;
            Q0=makeQuery(id+"F3.opExtrude","SWEPT_FACE",FACE,{"disambiguationData":[OSD([sQuery(id+"F2.wireOp",EDGE,"E1.top")])]});
            var Q1;
            Q1=makeQuery(id+"F3.opExtrude","SWEPT_FACE",FACE,{"disambiguationData":[OSD([sQuery(id+"F2.wireOp",EDGE,"E1.bottom")])]});
            cPlane(context, id + "F16", {"entities" : qUnion([Q0, Q1]), "cplaneType" : CPlaneType.MID_PLANE, "offset" : 25 * mm, "width" : 150 * mm, "height" : 150 * mm});
        }
        {
            var Q0;
            Q0=makeQuery(id+"F1.opExtrude","SWEPT_BODY",BODY,{"disambiguationData":[OSD([sQuery(id+"F0.wireOp",EDGE,"E0.bottom"),sQuery(id+"F0.wireOp",EDGE,"E0.top"),sQuery(id+"F0.wireOp",EDGE,"E0.left"),sQuery(id+"F0.wireOp",EDGE,"E0.right")])]});
            var Q1;
            Q1=qCreatedBy(id+"F16.planeOp",FACE);
            mirror(context, id + "F17", {"operationType" : NewBodyOperationType.ADD, "entities" : qUnion([Q0]), "mirrorPlane" : qUnion([Q1])});
        }
        {
            var Q0;
            Q0=makeQuery(id+"F7.opExtrude","SWEPT_FACE",FACE,{"disambiguationData":[OSD([sQuery(id+"F6.wireOp",EDGE,"E9.left")])]});
            var sketch = newSketch(context, id + "F18", { "sketchPlane" : qUnion([Q0])});
            skArc(sketch, "E73", {"start": v(-20, 6.3) * mm, "mid": v(-17.5, 3.8) * mm, "end": v(-15, 6.3) * mm});
            skLineSegment(sketch, "E74", {"start": v(-15, 6.3) * mm, "end": v(-15, 12.3) * mm});
            skLineSegment(sketch, "E75", {"start": v(-15, 12.3) * mm, "end": v(-20, 12.3) * mm});
            skLineSegment(sketch, "E76", {"start": v(-20, 12.3) * mm, "end": v(-20, 6.3) * mm});
            skArc(sketch, "E77.0.1.0", {"start": v(-20, 15.3) * mm, "mid": v(-17.5, 12.8) * mm, "end": v(-15, 15.3) * mm});
            skLineSegment(sketch, "E77.0.1.1", {"start": v(-15, 15.3) * mm, "end": v(-15, 21.3) * mm});
            skLineSegment(sketch, "E77.0.1.2", {"start": v(-15, 21.3) * mm, "end": v(-20, 21.3) * mm});
            skLineSegment(sketch, "E77.0.1.3", {"start": v(-20, 21.3) * mm, "end": v(-20, 15.3) * mm});
            skArc(sketch, "E77.0.2.0", {"start": v(-19.96, 23.87) * mm, "mid": v(-17.5, 21.8) * mm, "end": v(-15.04, 23.87) * mm});
            skArc(sketch, "E77.1.0.0", {"start": v(-14.5, 6.3) * mm, "mid": v(-12, 3.8) * mm, "end": v(-9.5, 6.3) * mm});
            skLineSegment(sketch, "E77.1.0.1", {"start": v(-9.5, 6.3) * mm, "end": v(-9.5, 12.3) * mm});
            skLineSegment(sketch, "E77.1.0.2", {"start": v(-9.5, 12.3) * mm, "end": v(-14.5, 12.3) * mm});
            skLineSegment(sketch, "E77.1.0.3", {"start": v(-14.5, 12.3) * mm, "end": v(-14.5, 6.3) * mm});
            skArc(sketch, "E77.1.1.0", {"start": v(-14.5, 15.3) * mm, "mid": v(-12.8, 12.92) * mm, "end": v(-10, 13.8) * mm});
            skLineSegment(sketch, "E77.1.1.2", {"start": v(-13.75, 21.3) * mm, "end": v(-14.5, 21.3) * mm});
            skLineSegment(sketch, "E77.1.1.3", {"start": v(-14.5, 21.3) * mm, "end": v(-14.5, 15.3) * mm});
            skArc(sketch, "E77.2.0.0", {"start": v(-9, 6.3) * mm, "mid": v(-7.72, 4.1) * mm, "end": v(-5.19, 4.16) * mm});
            skLineSegment(sketch, "E77.2.0.3", {"start": v(-9, 11.8) * mm, "end": v(-9, 6.3) * mm});
            skLineSegment(sketch, "E77.direction1", {"start": v(-20, 6.3) * mm, "end": v(-14.5, 6.3) * mm, "construction": true});
            skLineSegment(sketch, "E77.direction2", {"start": v(-20, 6.3) * mm, "end": v(-20, 15.3) * mm, "construction": true});
            skArc(sketch, "E78.MirrorCS", {"start": v(-20.5, 15.3) * mm, "mid": v(-22.2, 12.92) * mm, "end": v(-25, 13.8) * mm});
            skArc(sketch, "E79.MirrorCS", {"start": v(-20.5, 6.3) * mm, "mid": v(-23, 3.8) * mm, "end": v(-25.5, 6.3) * mm});
            skLineSegment(sketch, "E80.MirrorCS", {"start": v(-20.5, 12.3) * mm, "end": v(-20.5, 6.3) * mm});
            skLineSegment(sketch, "E81.MirrorCS", {"start": v(-26, 11.8) * mm, "end": v(-26, 6.3) * mm});
            skLineSegment(sketch, "E82.MirrorCS", {"start": v(-21.25, 21.3) * mm, "end": v(-20.5, 21.3) * mm});
            skArc(sketch, "E83.MirrorCS", {"start": v(-26, 6.3) * mm, "mid": v(-27.28, 4.1) * mm, "end": v(-29.81, 4.16) * mm});
            skLineSegment(sketch, "E84.MirrorCS", {"start": v(-25.5, 12.3) * mm, "end": v(-20.5, 12.3) * mm});
            skLineSegment(sketch, "E85.MirrorCS", {"start": v(-25.5, 6.3) * mm, "end": v(-25.5, 12.3) * mm});
            skLineSegment(sketch, "E86.MirrorCS", {"start": v(-20.5, 21.3) * mm, "end": v(-20.5, 15.3) * mm});
            skLineSegment(sketch, "E87", {"start": v(-29.81, 4.16) * mm, "end": v(-26, 11.8) * mm});
            skLineSegment(sketch, "E88", {"start": v(-18.45, 26.89) * mm, "end": v(-16.55, 26.89) * mm});
            skLineSegment(sketch, "E89", {"start": v(-16.55, 26.89) * mm, "end": v(-15.04, 23.87) * mm});
            skLineSegment(sketch, "E90.trimOffspring", {"start": v(-9, 11.8) * mm, "end": v(-5.19, 4.16) * mm});
            skLineSegment(sketch, "E91.trimOffspring", {"start": v(-13.75, 21.3) * mm, "end": v(-10, 13.8) * mm});
            skLineSegment(sketch, "E92.trimOffspring", {"start": v(-25, 13.8) * mm, "end": v(-21.25, 21.3) * mm});
            skLineSegment(sketch, "E93.trimOffspring", {"start": v(-19.96, 23.87) * mm, "end": v(-18.45, 26.89) * mm});
            skSolve(sketch);
        }
        {
            var Q0;
            Q0 = qSketchRegion(id + "F18", true);
            extrude(context, id + "F19", {"entities" : qUnion([Q0]), "operationType" : NewBodyOperationType.ADD, "depth" : 1 * mm, "offsetDistance" : 25 * mm});
        }
        {
            var Q0;
            Q0=makeQuery(id+"F1.opExtrude","CAP_FACE",FACE,{"disambiguationData":[OSD([sQuery(id+"F0.wireOp",EDGE,"E0.bottom"),sQuery(id+"F0.wireOp",EDGE,"E0.top"),sQuery(id+"F0.wireOp",EDGE,"E0.left"),sQuery(id+"F0.wireOp",EDGE,"E0.right")])],"isStart":true});
            extrude(context, id + "F20", {"entities" : qUnion([Q0]), "operationType" : NewBodyOperationType.ADD, "depth" : 10 * mm, "offsetDistance" : 25 * mm});
        }
        {
            var Q0;
            Q0=makeQuery(id+"F1.opExtrude","CAP_EDGE",EDGE,{"disambiguationData":[OSD([sQuery(id+"F0.wireOp",EDGE,"E0.bottom")])],"isStart":false});
            var Q1;
            Q1=makeQuery(id+"F1.opExtrude","CAP_EDGE",EDGE,{"disambiguationData":[OSD([sQuery(id+"F0.wireOp",EDGE,"E0.right")])],"isStart":false});
            var Q2;
            Q2=makeQuery(id+"F1.opExtrude","CAP_EDGE",EDGE,{"disambiguationData":[OSD([sQuery(id+"F0.wireOp",EDGE,"E0.left")])],"isStart":false});
            var Q3;
            Q3=makeQuery(id+"F1.opExtrude","CAP_EDGE",EDGE,{"disambiguationData":[OSD([sQuery(id+"F0.wireOp",EDGE,"E0.top")])],"isStart":false});
            chamfer(context, id + "F21", {"entities" : qUnion([Q0, Q1, Q2, Q3]), "width" : 1.5 * mm, "tangentPropagation" : true});
        }
        {
            var Q0;
            Q0=makeQuery(id+"F3.opExtrude","CAP_EDGE",EDGE,{"disambiguationData":[OSD([sQuery(id+"F2.wireOp",EDGE,"E1.top")])],"isStart":false});
            var Q1;
            Q1=makeQuery(id+"F3.opExtrude","CAP_EDGE",EDGE,{"disambiguationData":[OSD([sQuery(id+"F2.wireOp",EDGE,"E1.right")])],"isStart":false});
            var Q2;
            Q2=makeQuery(id+"F3.opExtrude","CAP_EDGE",EDGE,{"disambiguationData":[OSD([sQuery(id+"F2.wireOp",EDGE,"E1.bottom")])],"isStart":false});
            var Q3;
            Q3=makeQuery(id+"F3.opExtrude","CAP_EDGE",EDGE,{"disambiguationData":[OSD([sQuery(id+"F2.wireOp",EDGE,"E1.left")])],"isStart":false});
            chamfer(context, id + "F22", {"entities" : qUnion([Q0, Q1, Q2, Q3]), "width" : 1.5 * mm, "tangentPropagation" : true});
        }
        {
            var Q0;
            {var subQ0=sQuery(id+"F0.wireOp",EDGE,"E0.bottom");Q0=makeQuery(id+"F20.boolean.opBoolean","MERGE",FACE,{"derivedFrom":[makeQuery(id+"F1.opExtrude","SWEPT_FACE",FACE,{"disambiguationData":[OSD([subQ0])]}),makeQuery(id+"F20.opExtrude","SWEPT_FACE",FACE,{"disambiguationData":[OSD([subQ0])]})]});}
            var sketch = newSketch(context, id + "F23", { "sketchPlane" : qUnion([Q0])});
            skText(sketch, "E94", { "text": "Mulțumim Pentru Tot!", "fontName": "RobotoSlab-Bold.ttf"});
            skText(sketch, "E95", { "text": "Alex | Katja | Lorena", "fontName": "RobotoSlab-Regular.ttf"});
            const initialGuessF23  = {"E94": [-0.0796, -0.0015, 1, 0, 0.004], "E95": [-0.06628, -0.007, 1, 0, 0.0025]};
            skSetInitialGuess(sketch, initialGuessF23);
            skSolve(sketch);
        }
        {
            var Q0;
            Q0 = qSketchRegion(id + "F23", true);
            var Q1;
            {var subQ0=sQuery(id+"F0.wireOp",EDGE,"E0.top");Q1=makeQuery(id+"F20.boolean.opBoolean","MERGE",FACE,{"derivedFrom":[makeQuery(id+"F1.opExtrude","SWEPT_FACE",FACE,{"disambiguationData":[OSD([subQ0])]}),makeQuery(id+"F20.opExtrude","SWEPT_FACE",FACE,{"disambiguationData":[OSD([subQ0])]})]});}
            extrude(context, id + "F24", {"entities" : qUnion([Q0]), "operationType" : NewBodyOperationType.REMOVE, "oppositeDirection" : true, "depth" : 1.5 * mm, "endBoundEntityFace" : qUnion([Q1]), "offsetDistance" : 25 * mm});
        }
    });
